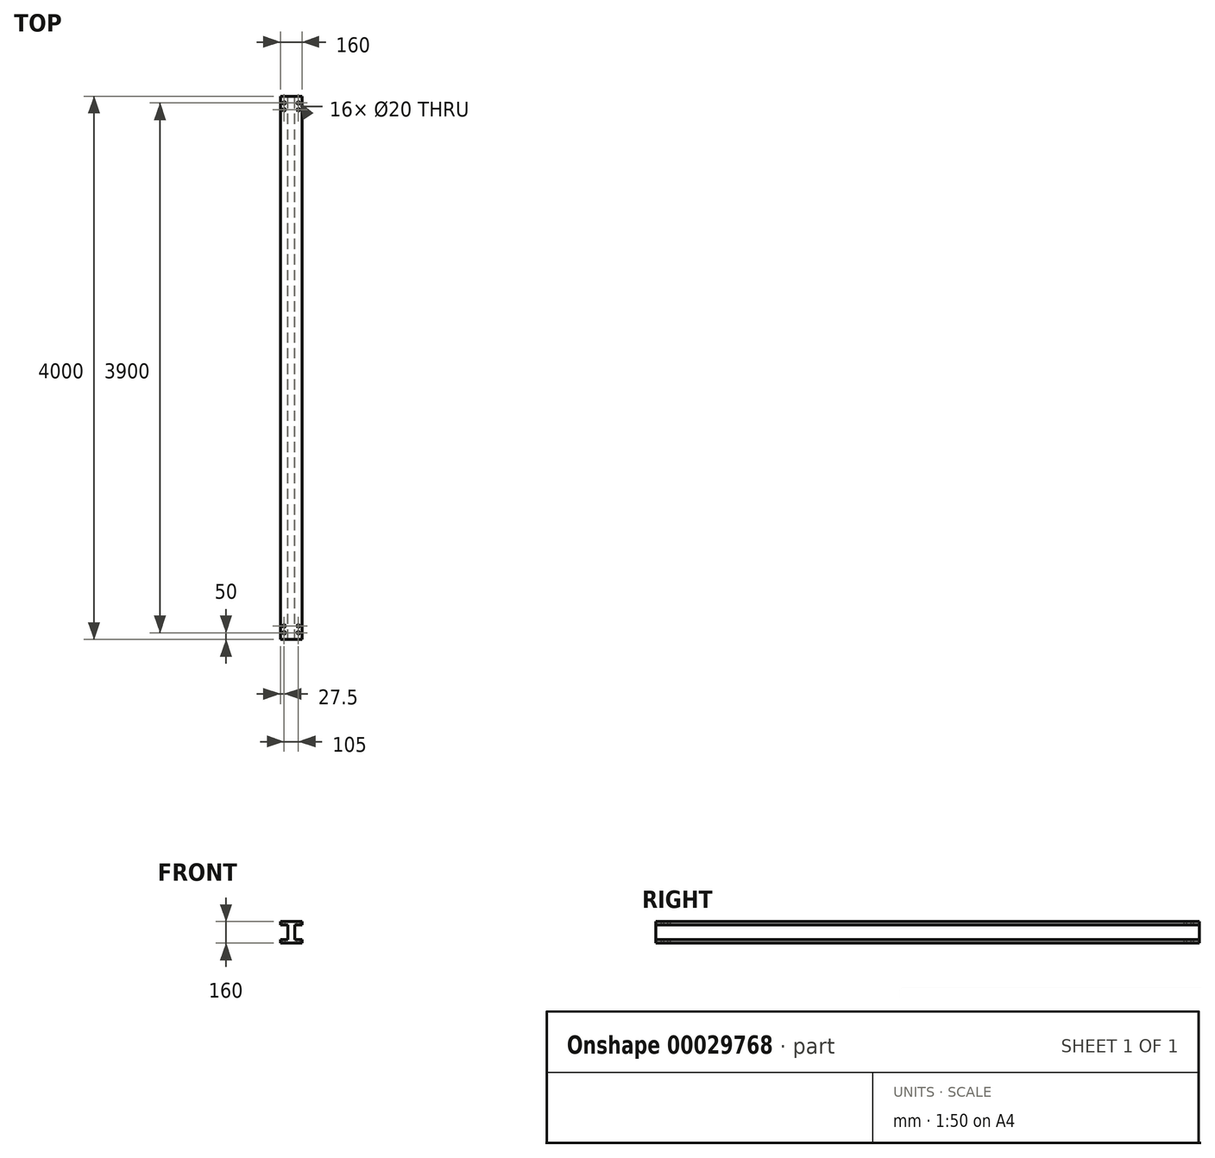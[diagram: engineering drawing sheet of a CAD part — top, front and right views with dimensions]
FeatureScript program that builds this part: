
annotation { "Feature Type Name" : "Feature", "Feature Type Description" : "" }
export const myFeature = defineFeature(function(context is Context, id is Id, definition is map)
    precondition{}
    {
        {
            var Q0;
            Q0=qCreatedBy(makeId("Front.planeOp"),FACE);
            var sketch = newSketch(context, id + "F0", { "sketchPlane" : qUnion([Q0])});
            skLineSegment(sketch, "E0", {"start": v(-25, 55) * mm, "end": v(-25, -55) * mm});
            skLineSegment(sketch, "E1", {"start": v(25, 55) * mm, "end": v(25, -55) * mm});
            skLineSegment(sketch, "E2", {"start": v(-80, 80) * mm, "end": v(-80, 55) * mm});
            skLineSegment(sketch, "E3", {"start": v(-80, 55) * mm, "end": v(-25, 55) * mm});
            skLineSegment(sketch, "E4", {"start": v(80, 55) * mm, "end": v(80, 80) * mm});
            skLineSegment(sketch, "E5", {"start": v(-80, -80) * mm, "end": v(-80, -55) * mm});
            skLineSegment(sketch, "E6", {"start": v(-80, -55) * mm, "end": v(-25, -55) * mm});
            skLineSegment(sketch, "E7", {"start": v(80, -55) * mm, "end": v(80, -80) * mm});
            skLineSegment(sketch, "E8", {"start": v(-80, 80) * mm, "end": v(80, 80) * mm});
            skLineSegment(sketch, "E9", {"start": v(-80, -80) * mm, "end": v(80, -80) * mm});
            skLineSegment(sketch, "E10.trimOffspring", {"start": v(25, 55) * mm, "end": v(80, 55) * mm});
            skLineSegment(sketch, "E11.trimOffspring", {"start": v(25, -55) * mm, "end": v(80, -55) * mm});
            skSolve(sketch);
        }
        {
            var Q0;
            Q0 = qSketchRegion(id + "F0", true);
            extrude(context, id + "F1", {"entities" : qUnion([Q0]), "depth" : 4000 * mm});
        }
        {
            var Q0;
            Q0=makeQuery(id+"F1.opExtrude","SWEPT_FACE",FACE,{"disambiguationData":[OSD([sQuery(id+"F0.wireOp",EDGE,"E8")])]});
            var sketch = newSketch(context, id + "F2", { "sketchPlane" : qUnion([Q0])});
            skCircle(sketch, "E12", {"center": v(-52.5, -3950) * mm, "radius": 10 * mm});
            skCircle(sketch, "E13", {"center": v(-52.5, -3900) * mm, "radius": 10 * mm});
            skCircle(sketch, "E14", {"center": v(52.5, -3900) * mm, "radius": 10 * mm});
            skCircle(sketch, "E15", {"center": v(52.5, -3950) * mm, "radius": 10 * mm});
            skSolve(sketch);
        }
        {
            var Q0;
            Q0 = qSketchRegion(id + "F2", true);
            extrude(context, id + "F3", {"entities" : qUnion([Q0]), "operationType" : NewBodyOperationType.REMOVE, "oppositeDirection" : true, "depth" : 160 * mm});
        }
        {
            var Q0;
            Q0=makeQuery(id+"F1.opExtrude","SWEPT_FACE",FACE,{"disambiguationData":[OSD([sQuery(id+"F0.wireOp",EDGE,"E8")])]});
            var sketch = newSketch(context, id + "F4", { "sketchPlane" : qUnion([Q0])});
            skCircle(sketch, "E16", {"center": v(52.5, -50) * mm, "radius": 10 * mm});
            skCircle(sketch, "E17", {"center": v(-52.5, -50) * mm, "radius": 10 * mm});
            skCircle(sketch, "E18", {"center": v(-52.5, -100) * mm, "radius": 10 * mm});
            skCircle(sketch, "E19", {"center": v(52.5, -100) * mm, "radius": 10 * mm});
            skSolve(sketch);
        }
        {
            var Q0;
            Q0 = qSketchRegion(id + "F4", true);
            extrude(context, id + "F5", {"entities" : qUnion([Q0]), "operationType" : NewBodyOperationType.REMOVE, "oppositeDirection" : true, "depth" : 160 * mm});
        }
    });
